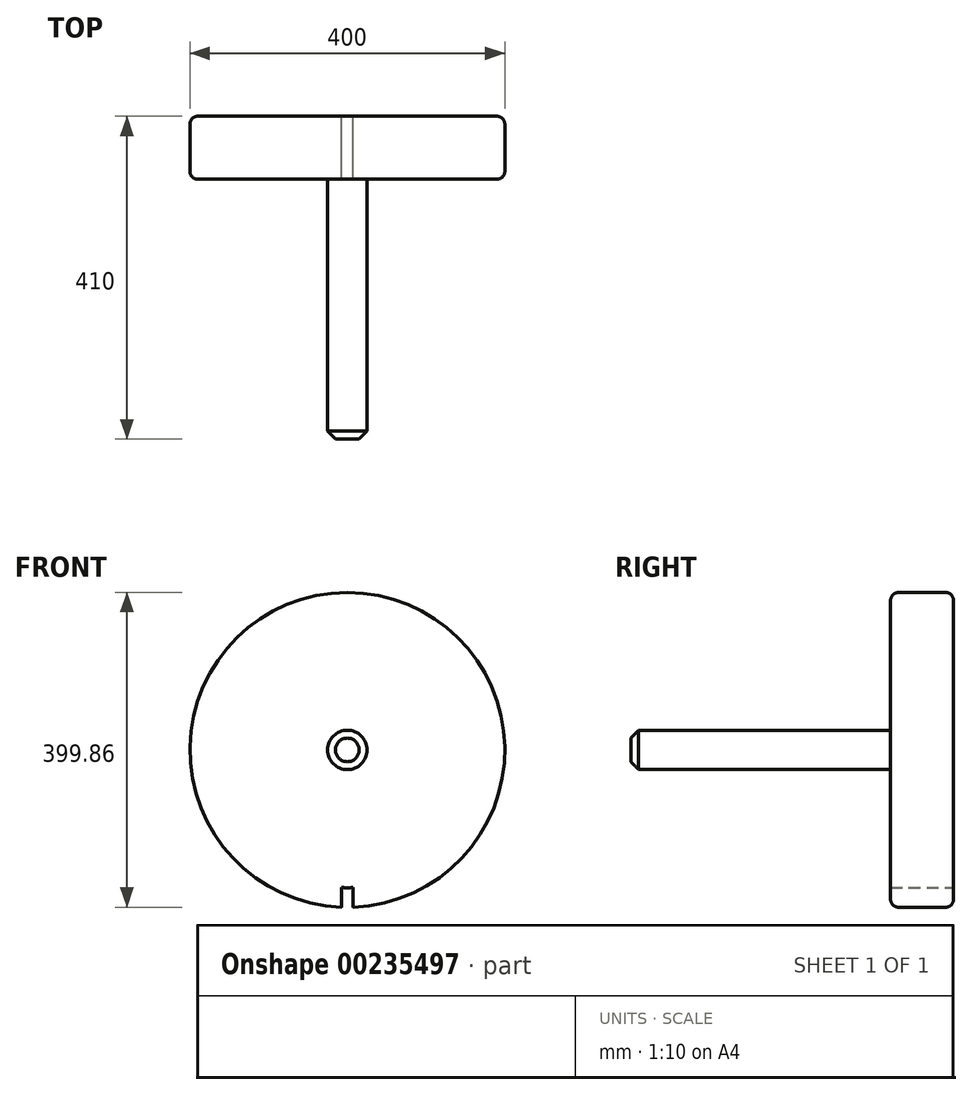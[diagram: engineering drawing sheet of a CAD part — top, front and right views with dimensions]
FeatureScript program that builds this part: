
annotation { "Feature Type Name" : "Feature", "Feature Type Description" : "" }
export const myFeature = defineFeature(function(context is Context, id is Id, definition is map)
    precondition{}
    {
        {
            var Q0;
            Q0=qCreatedBy(makeId("Front.planeOp"),FACE);
            var sketch = newSketch(context, id + "F0", { "sketchPlane" : qUnion([Q0])});
            skCircle(sketch, "E0", {"center": v(0, 0) * mm, "radius": 200 * mm});
            skCircle(sketch, "E1", {"center": v(0, 0) * mm, "radius": 175 * mm});
            skCircle(sketch, "E2", {"center": v(0, 0) * mm, "radius": 25 * mm});
            skSolve(sketch);
        }
        {
            var Q0;
            Q0=makeQuery(id+"F0.imprint","IMPRINT",FACE,{"disambiguationData":[TD([[makeQuery(id+"F0.imprint","IMPRINT",EDGE,{"derivedFrom":sQuery(id+"F0.wireOp",EDGE,"E0")}),1.0]])]});
            var Q1;
            Q1=makeQuery(id+"F0.imprint","IMPRINT",FACE,{"disambiguationData":[TD([[makeQuery(id+"F0.imprint","IMPRINT",EDGE,{"derivedFrom":sQuery(id+"F0.wireOp",EDGE,"E1")}),1.0]])]});
            extrude(context, id + "F1", {"entities" : qUnion([Q0, Q1]), "depth" : 80 * mm});
        }
        {
            var Q0;
            Q0=makeQuery(id+"F0.imprint","IMPRINT",FACE,{"disambiguationData":[TD([[makeQuery(id+"F0.imprint","IMPRINT",EDGE,{"derivedFrom":sQuery(id+"F0.wireOp",EDGE,"E2")}),1.0]])]});
            extrude(context, id + "F2", {"entities" : qUnion([Q0]), "operationType" : NewBodyOperationType.ADD, "depth" : 410 * mm});
        }
        {
            var Q0;
            Q0=makeQuery(id+"F1.opExtrude","CAP_EDGE",EDGE,{"disambiguationData":[OSD([sQuery(id+"F0.wireOp",EDGE,"E0")])],"isStart":true});
            var Q1;
            Q1=makeQuery(id+"F1.opExtrude","CAP_EDGE",EDGE,{"disambiguationData":[OSD([sQuery(id+"F0.wireOp",EDGE,"E0")])],"isStart":false});
            var Q2;
            Q2=makeQuery(id+"F1.opExtrude","CAP_EDGE",EDGE,{"disambiguationData":[OSD([sQuery(id+"F0.wireOp",EDGE,"E2")])],"isStart":false});
            fillet(context, id + "F3", {"entities" : qUnion([Q0, Q1, Q2]), "radius" : 10 * mm, "tangentPropagation" : true, "allowEdgeOverflow" : false});
        }
        {
            var Q0;
            Q0=makeQuery(id+"F2.opExtrude","CAP_EDGE",EDGE,{"disambiguationData":[OSD([sQuery(id+"F0.wireOp",EDGE,"E2")])],"isStart":false});
            chamfer(context, id + "F4", {"entities" : qUnion([Q0]), "width" : 10 * mm, "tangentPropagation" : true});
        }
        {
            var Q0;
            Q0=qCreatedBy(makeId("Front.planeOp"),FACE);
            var sketch = newSketch(context, id + "F5", { "sketchPlane" : qUnion([Q0])});
            skArc(sketch, "E3.0.0", {"start": v(-7.5, -174.84) * mm, "mid": v(0, -175) * mm, "end": v(7.5, -174.84) * mm});
            skLineSegment(sketch, "E4.bottom", {"start": v(-7.5, -213.87) * mm, "end": v(7.5, -213.87) * mm});
            skLineSegment(sketch, "E4.top", {"start": v(-7.5, -174.84) * mm, "end": v(7.5, -174.84) * mm});
            skLineSegment(sketch, "E4.left", {"start": v(-7.5, -213.87) * mm, "end": v(-7.5, -174.84) * mm});
            skLineSegment(sketch, "E4.right", {"start": v(7.5, -213.87) * mm, "end": v(7.5, -174.84) * mm});
            skSolve(sketch);
        }
        {
            var Q0;
            Q0=makeQuery(id+"F5.imprint","IMPRINT",FACE,{"disambiguationData":[TD([[makeQuery(id+"F5.imprint","IMPRINT",EDGE,{"derivedFrom":sQuery(id+"F5.wireOp",EDGE,"E3.0.0")}),-1.0]])]});
            extrude(context, id + "F6", {"entities" : qUnion([Q0]), "operationType" : NewBodyOperationType.REMOVE, "endBound" : BoundingType.THROUGH_ALL, "depth" : 25 * mm});
        }
    });
